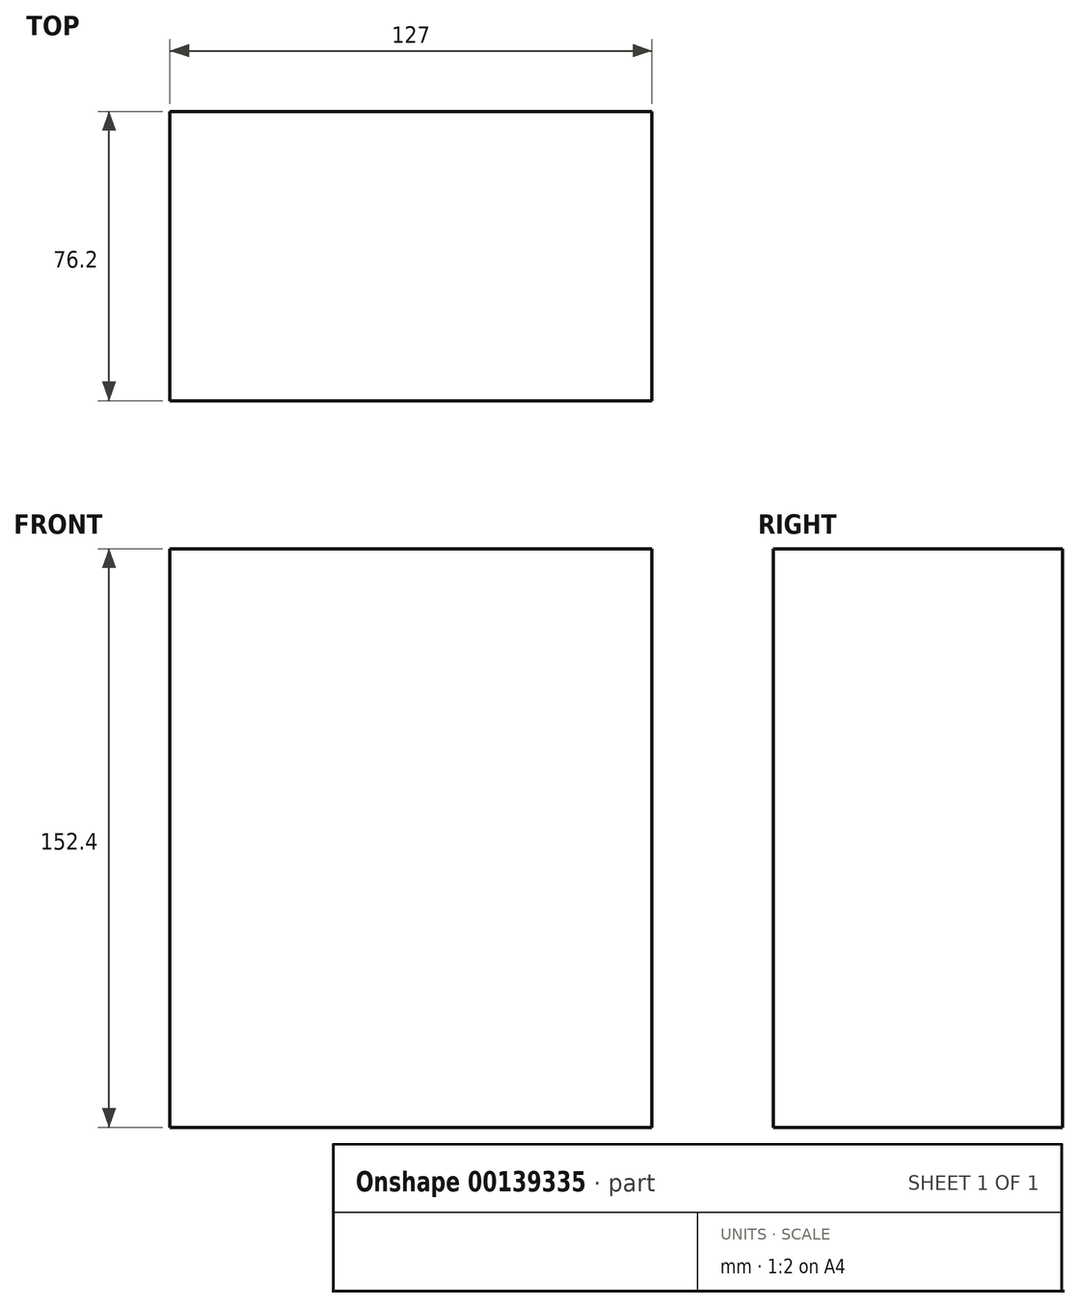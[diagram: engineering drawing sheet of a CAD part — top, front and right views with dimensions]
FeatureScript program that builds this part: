
annotation { "Feature Type Name" : "Feature", "Feature Type Description" : "" }
export const myFeature = defineFeature(function(context is Context, id is Id, definition is map)
    precondition{}
    {
        {
            var Q0;
            Q0=qCreatedBy(makeId("Top.planeOp"),FACE);
            var sketch = newSketch(context, id + "F1", { "sketchPlane" : qUnion([Q0])});
            skLineSegment(sketch, "E0.bottom", {"start": v(0, 76.2) * mm, "end": v(127, 76.2) * mm});
            skLineSegment(sketch, "E0.top", {"start": v(0, 0) * mm, "end": v(127, 0) * mm});
            skLineSegment(sketch, "E0.left", {"start": v(0, 76.2) * mm, "end": v(0, 0) * mm});
            skLineSegment(sketch, "E0.right", {"start": v(127, 76.2) * mm, "end": v(127, 0) * mm});
            skLineSegment(sketch, "E1.bottom", {"start": v(-127, 431.8) * mm, "end": v(127, 431.8) * mm});
            skLineSegment(sketch, "E1.top", {"start": v(-127, 76.2) * mm, "end": v(127, 76.2) * mm});
            skLineSegment(sketch, "E1.left", {"start": v(-127, 431.8) * mm, "end": v(-127, 76.2) * mm});
            skLineSegment(sketch, "E1.right", {"start": v(127, 431.8) * mm, "end": v(127, 76.2) * mm});
            skLineSegment(sketch, "E2.bottom", {"start": v(25.6, -25.4) * mm, "end": v(101.8, -25.4) * mm});
            skLineSegment(sketch, "E2.top", {"start": v(25.6, 0) * mm, "end": v(101.8, 0) * mm});
            skLineSegment(sketch, "E2.left", {"start": v(25.6, -25.4) * mm, "end": v(25.6, 0) * mm});
            skLineSegment(sketch, "E2.right", {"start": v(101.8, -25.4) * mm, "end": v(101.8, 0) * mm});
            skLineSegment(sketch, "E3.bottom", {"start": v(-38.1, 0) * mm, "end": v(0, 0) * mm});
            skLineSegment(sketch, "E3.top", {"start": v(-38.1, 76.2) * mm, "end": v(0, 76.2) * mm});
            skLineSegment(sketch, "E3.left", {"start": v(-38.1, 0) * mm, "end": v(-38.1, 76.2) * mm});
            skLineSegment(sketch, "E3.right", {"start": v(0, 0) * mm, "end": v(0, 76.2) * mm});
            skLineSegment(sketch, "E4.bottom", {"start": v(-127, 0) * mm, "end": v(-38.1, 0) * mm});
            skLineSegment(sketch, "E4.top", {"start": v(-127, 76.2) * mm, "end": v(-38.1, 76.2) * mm});
            skLineSegment(sketch, "E4.left", {"start": v(-127, 0) * mm, "end": v(-127, 76.2) * mm});
            skSolve(sketch);
        }
        {
            var Q0;
            {var subQ0=sQuery(id+"F1.wireOp",EDGE,"E0.right");Q0=makeQuery(id+"F1.imprint","IMPRINT",FACE,{"disambiguationData":[TD([[makeQuery(id+"F1.imprint","IMPRINT",EDGE,{"derivedFrom":subQ0}),-1.0]])]});}
            extrude(context, id + "F0", {"entities" : qUnion([Q0]), "depth" : 152.4 * mm});
        }
    });
